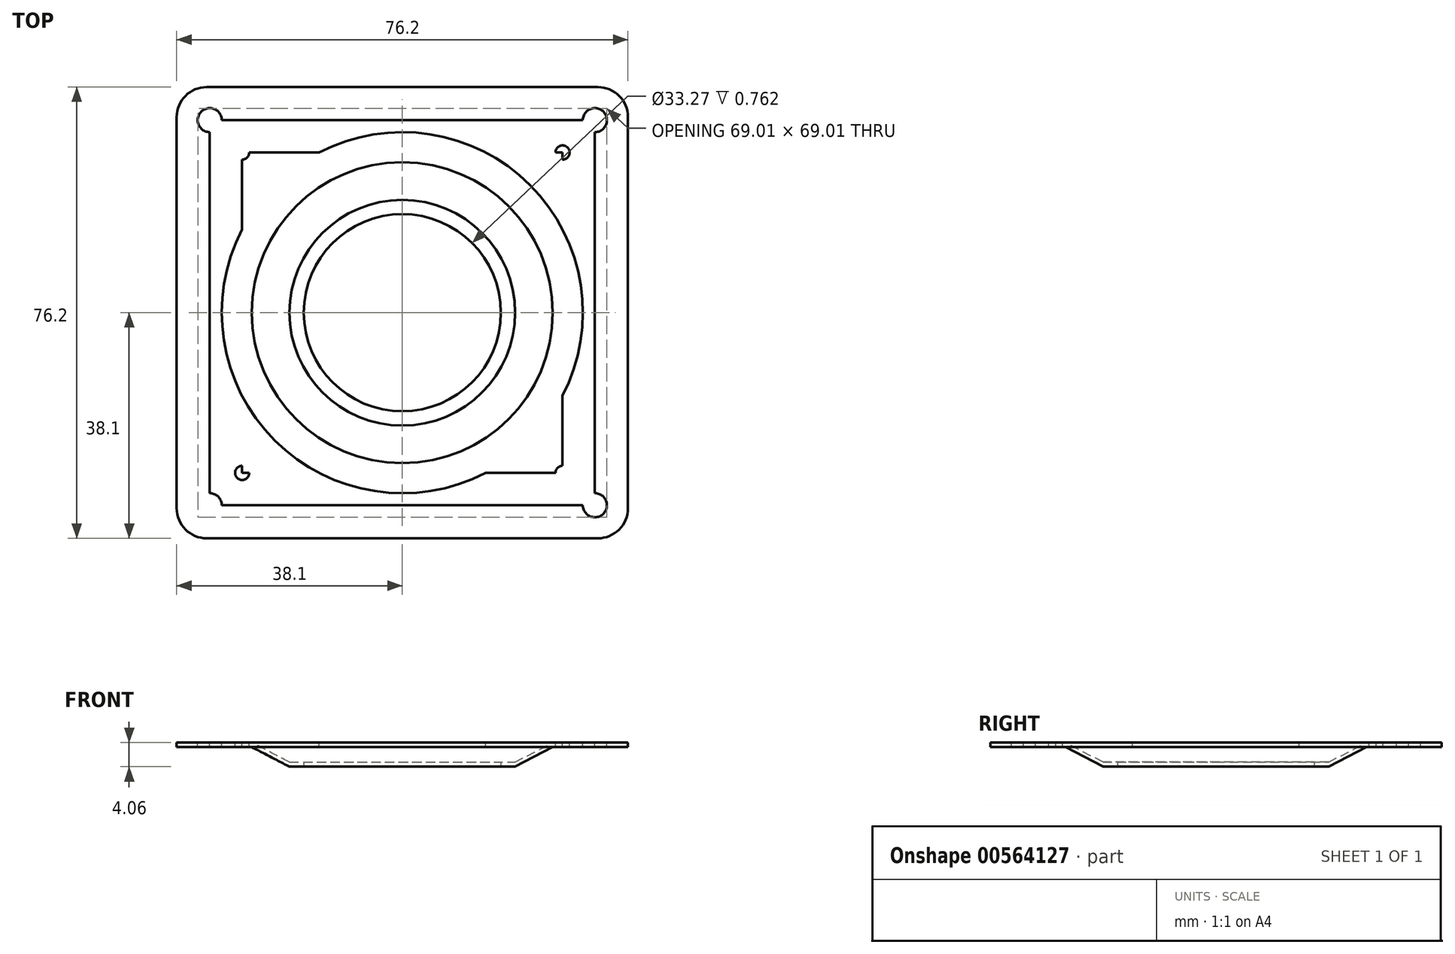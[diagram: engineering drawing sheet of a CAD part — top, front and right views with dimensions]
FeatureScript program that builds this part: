
annotation { "Feature Type Name" : "Feature", "Feature Type Description" : "" }
export const myFeature = defineFeature(function(context is Context, id is Id, definition is map)
    precondition{}
    {
        {
            var Q0;
            Q0=qCreatedBy(makeId("Right.planeOp"),FACE);
            var sketch = newSketch(context, id + "F0", { "sketchPlane" : qUnion([Q0])});
            skLineSegment(sketch, "E0", {"start": v(0, -4.38) * mm, "end": v(0, 4.93) * mm});
            skLineSegment(sketch, "E1.bottom", {"start": v(-16.64, 0) * mm, "end": v(-19.05, 0) * mm});
            skLineSegment(sketch, "E1.top", {"start": v(-16.64, 0.76) * mm, "end": v(-19.05, 0.76) * mm});
            skLineSegment(sketch, "E1.left", {"start": v(-16.64, 0) * mm, "end": v(-16.64, 0.76) * mm});
            skLineSegment(sketch, "E1.right", {"start": v(-19.05, 0) * mm, "end": v(-19.05, 0.76) * mm});
            skLineSegment(sketch, "E2.bottom", {"start": v(-30.48, 4.06) * mm, "end": v(-25.4, 4.06) * mm});
            skLineSegment(sketch, "E2.top", {"start": v(-30.48, 3.3) * mm, "end": v(-25.4, 3.3) * mm});
            skLineSegment(sketch, "E2.left", {"start": v(-30.48, 4.06) * mm, "end": v(-30.48, 3.3) * mm});
            skLineSegment(sketch, "E2.right", {"start": v(-25.4, 4.06) * mm, "end": v(-25.4, 3.3) * mm});
            skLineSegment(sketch, "E3", {"start": v(-25.4, 4.06) * mm, "end": v(-19.05, 0.76) * mm});
            skLineSegment(sketch, "E4", {"start": v(-19.05, 0) * mm, "end": v(-25.4, 3.3) * mm});
            skSolve(sketch);
        }
        {
            var Q0;
            Q0=makeQuery(id+"F0.imprint","IMPRINT",FACE,{"disambiguationData":[TD([[makeQuery(id+"F0.imprint","IMPRINT",EDGE,{"derivedFrom":sQuery(id+"F0.wireOp",EDGE,"E2.bottom")}),-1.0]])]});
            var Q1;
            Q1=makeQuery(id+"F0.imprint","IMPRINT",FACE,{"disambiguationData":[TD([[makeQuery(id+"F0.imprint","IMPRINT",EDGE,{"derivedFrom":sQuery(id+"F0.wireOp",EDGE,"E1.right")}),1.0]])]});
            var Q2;
            Q2=makeQuery(id+"F0.imprint","IMPRINT",FACE,{"disambiguationData":[TD([[makeQuery(id+"F0.imprint","IMPRINT",EDGE,{"derivedFrom":sQuery(id+"F0.wireOp",EDGE,"E1.bottom")}),-1.0]])]});
            var Q3;
            Q3=sQuery(id+"F0.wireOp",EDGE,"E0");
            revolve(context, id + "F1", {"entities" : qUnion([Q0, Q1, Q2]), "axis" : qUnion([Q3]), "revolveType" : RevolveType.FULL});
        }
        {
            var Q0;
            Q0=makeQuery(id+"F1.opRevolve","SWEPT_FACE",FACE,{"disambiguationData":[OSD([sQuery(id+"F0.wireOp",EDGE,"E2.bottom")])]});
            var sketch = newSketch(context, id + "F2", { "sketchPlane" : qUnion([Q0])});
            skLineSegment(sketch, "E5.bottom", {"start": v(-38.1, 38.1) * mm, "end": v(38.1, 38.1) * mm});
            skLineSegment(sketch, "E5.top", {"start": v(-38.1, -38.1) * mm, "end": v(38.1, -38.1) * mm});
            skLineSegment(sketch, "E5.left", {"start": v(-38.1, 38.1) * mm, "end": v(-38.1, -38.1) * mm});
            skLineSegment(sketch, "E5.right", {"start": v(38.1, 38.1) * mm, "end": v(38.1, -38.1) * mm});
            skPoint(sketch, "E5.middle", {"position": v(0, 0) * mm});
            skLineSegment(sketch, "E6.bottom", {"start": v(-32.51, 32.51) * mm, "end": v(32.51, 32.51) * mm});
            skLineSegment(sketch, "E6.top", {"start": v(-32.51, -32.51) * mm, "end": v(32.51, -32.51) * mm});
            skLineSegment(sketch, "E6.left", {"start": v(-32.51, 32.51) * mm, "end": v(-32.51, -32.51) * mm});
            skLineSegment(sketch, "E6.right", {"start": v(32.51, 32.51) * mm, "end": v(32.51, -32.51) * mm});
            skLineSegment(sketch, "E7.bottom", {"start": v(-27.05, 27.05) * mm, "end": v(27.05, 27.05) * mm});
            skLineSegment(sketch, "E7.top", {"start": v(-27.05, -27.05) * mm, "end": v(27.05, -27.05) * mm});
            skLineSegment(sketch, "E7.left", {"start": v(-27.05, 27.05) * mm, "end": v(-27.05, -27.05) * mm});
            skLineSegment(sketch, "E7.right", {"start": v(27.05, 27.05) * mm, "end": v(27.05, -27.05) * mm});
            skLineSegment(sketch, "E8", {"start": v(-38.1, 38.1) * mm, "end": v(0, 0) * mm});
            skCircle(sketch, "E9", {"center": v(-27.05, 27.05) * mm, "radius": 1.2 * mm});
            skCircle(sketch, "E10", {"center": v(-32.51, 32.51) * mm, "radius": 2.03 * mm});
            skLineSegment(sketch, "E11", {"start": v(0, 5.12) * mm, "end": v(0, -5.17) * mm});
            skLineSegment(sketch, "E12", {"start": v(-5.34, 0) * mm, "end": v(6.02, 0) * mm});
            skCircle(sketch, "E13.MirrorC", {"center": v(27.05, 27.05) * mm, "radius": 1.2 * mm});
            skCircle(sketch, "E14.MirrorC", {"center": v(32.51, 32.51) * mm, "radius": 2.03 * mm});
            skCircle(sketch, "E15.MirrorC", {"center": v(-32.51, -32.51) * mm, "radius": 2.03 * mm});
            skCircle(sketch, "E16.MirrorC", {"center": v(-27.05, -27.05) * mm, "radius": 1.2 * mm});
            skCircle(sketch, "E17.MirrorC", {"center": v(27.05, -27.05) * mm, "radius": 1.2 * mm});
            skCircle(sketch, "E18.MirrorC", {"center": v(32.51, -32.51) * mm, "radius": 2.03 * mm});
            skSolve(sketch);
        }
        {
            var Q0;
            {var subQ0=sQuery(id+"F2.wireOp",EDGE,"E15.MirrorC");var subQ5=sQuery(id+"F2.wireOp",EDGE,"E6.top");var subQ6=makeQuery(id+"F2.imprint","INTERSECT",VERTEX,{"derivedFrom":[subQ5,subQ0]});Q0=makeQuery(id+"F2.imprint","IMPRINT",FACE,{"disambiguationData":[TD([[makeQuery(id+"F2.imprint","IMPRINT",EDGE,{"disambiguationData":[TD([[subQ6,-1.0]])],"derivedFrom":subQ0}),1.0]])]});}
            var Q1;
            {var subQ0=sQuery(id+"F2.wireOp",EDGE,"E15.MirrorC");var subQ1=sQuery(id+"F2.wireOp",EDGE,"E6.top");var subQ2=makeQuery(id+"F2.imprint","INTERSECT",VERTEX,{"derivedFrom":[subQ1,subQ0]});Q1=makeQuery(id+"F2.imprint","IMPRINT",FACE,{"disambiguationData":[TD([[makeQuery(id+"F2.imprint","IMPRINT",EDGE,{"disambiguationData":[TD([[subQ2,1.0]])],"derivedFrom":subQ0}),1.0]])]});}
            var Q2;
            {var subQ0=sQuery(id+"F2.wireOp",EDGE,"E10");var subQ1=sQuery(id+"F2.wireOp",EDGE,"E6.left");var subQ2=makeQuery(id+"F2.imprint","INTERSECT",VERTEX,{"derivedFrom":[subQ1,subQ0]});Q2=makeQuery(id+"F2.imprint","IMPRINT",FACE,{"disambiguationData":[TD([[makeQuery(id+"F2.imprint","IMPRINT",EDGE,{"disambiguationData":[TD([[subQ2,1.0]])],"derivedFrom":subQ0}),-1.0]])]});}
            var Q3;
            {var subQ0=sQuery(id+"F2.wireOp",EDGE,"E17.MirrorC");var subQ1=sQuery(id+"F2.wireOp",EDGE,"E7.top");var subQ2=makeQuery(id+"F2.imprint","INTERSECT",VERTEX,{"derivedFrom":[subQ1,subQ0]});Q3=makeQuery(id+"F2.imprint","IMPRINT",FACE,{"disambiguationData":[TD([[makeQuery(id+"F2.imprint","IMPRINT",EDGE,{"disambiguationData":[TD([[subQ2,1.0]])],"derivedFrom":subQ0}),-1.0]])]});}
            var Q4;
            {var subQ0=sQuery(id+"F2.wireOp",EDGE,"E13.MirrorC");var subQ1=sQuery(id+"F2.wireOp",EDGE,"E7.bottom");var subQ2=makeQuery(id+"F2.imprint","INTERSECT",VERTEX,{"derivedFrom":[subQ1,subQ0]});Q4=makeQuery(id+"F2.imprint","IMPRINT",FACE,{"disambiguationData":[TD([[makeQuery(id+"F2.imprint","IMPRINT",EDGE,{"disambiguationData":[TD([[subQ2,1.0]])],"derivedFrom":subQ0}),1.0]])]});}
            var Q5;
            {var subQ0=sQuery(id+"F2.wireOp",EDGE,"E9");var subQ1=sQuery(id+"F2.wireOp",EDGE,"E7.left");var subQ2=makeQuery(id+"F2.imprint","INTERSECT",VERTEX,{"derivedFrom":[subQ1,subQ0]});Q5=makeQuery(id+"F2.imprint","IMPRINT",FACE,{"disambiguationData":[TD([[makeQuery(id+"F2.imprint","IMPRINT",EDGE,{"disambiguationData":[TD([[subQ2,-1.0]])],"derivedFrom":subQ0}),-1.0]])]});}
            var Q6;
            {var subQ0=sQuery(id+"F2.wireOp",EDGE,"E16.MirrorC");var subQ1=sQuery(id+"F2.wireOp",EDGE,"E7.top");var subQ2=makeQuery(id+"F2.imprint","INTERSECT",VERTEX,{"derivedFrom":[subQ1,subQ0]});Q6=makeQuery(id+"F2.imprint","IMPRINT",FACE,{"disambiguationData":[TD([[makeQuery(id+"F2.imprint","IMPRINT",EDGE,{"disambiguationData":[TD([[subQ2,1.0]])],"derivedFrom":subQ0}),1.0]])]});}
            var Q7;
            {var subQ0=sQuery(id+"F2.wireOp",EDGE,"E9");var subQ1=sQuery(id+"F2.wireOp",EDGE,"E7.bottom");var subQ2=makeQuery(id+"F2.imprint","INTERSECT",VERTEX,{"derivedFrom":[subQ1,subQ0]});Q7=makeQuery(id+"F2.imprint","IMPRINT",FACE,{"disambiguationData":[TD([[makeQuery(id+"F2.imprint","IMPRINT",EDGE,{"disambiguationData":[TD([[subQ2,1.0]])],"derivedFrom":subQ0}),-1.0]])]});}
            var Q8;
            Q8=makeQuery(id+"F1.opRevolve","SWEPT_FACE",FACE,{"disambiguationData":[OSD([sQuery(id+"F0.wireOp",EDGE,"E2.top")])]});
            extrude(context, id + "F3", {"entities" : qUnion([Q0, Q1, Q2, Q3, Q4, Q5, Q6, Q7]), "operationType" : NewBodyOperationType.ADD, "endBound" : BoundingType.UP_TO_SURFACE, "oppositeDirection" : true, "depth" : 25.4 * mm, "endBoundEntityFace" : qUnion([Q8]), "offsetDistance" : 25.4 * mm});
        }
        {
            var Q0;
            Q0=makeQuery(id+"F3.opExtrude","SWEPT_EDGE",EDGE,{"disambiguationData":[OSD([sQuery(id+"F2.wireOp",EDGE,"E5.top"),sQuery(id+"F2.wireOp",EDGE,"E5.left")])]});
            var Q1;
            Q1=makeQuery(id+"F3.opExtrude","SWEPT_EDGE",EDGE,{"disambiguationData":[OSD([sQuery(id+"F2.wireOp",EDGE,"E5.top"),sQuery(id+"F2.wireOp",EDGE,"E5.right")])]});
            var Q2;
            Q2=makeQuery(id+"F3.opExtrude","SWEPT_EDGE",EDGE,{"disambiguationData":[OSD([sQuery(id+"F2.wireOp",EDGE,"E5.bottom"),sQuery(id+"F2.wireOp",EDGE,"E5.left")])]});
            var Q3;
            Q3=makeQuery(id+"F3.opExtrude","SWEPT_EDGE",EDGE,{"disambiguationData":[OSD([sQuery(id+"F2.wireOp",EDGE,"E5.bottom"),sQuery(id+"F2.wireOp",EDGE,"E5.right")])]});
            fillet(context, id + "F4", {"entities" : qUnion([Q0, Q1, Q2, Q3]), "radius" : 5.08 * mm, "tangentPropagation" : true, "allowEdgeOverflow" : false});
        }
    });
